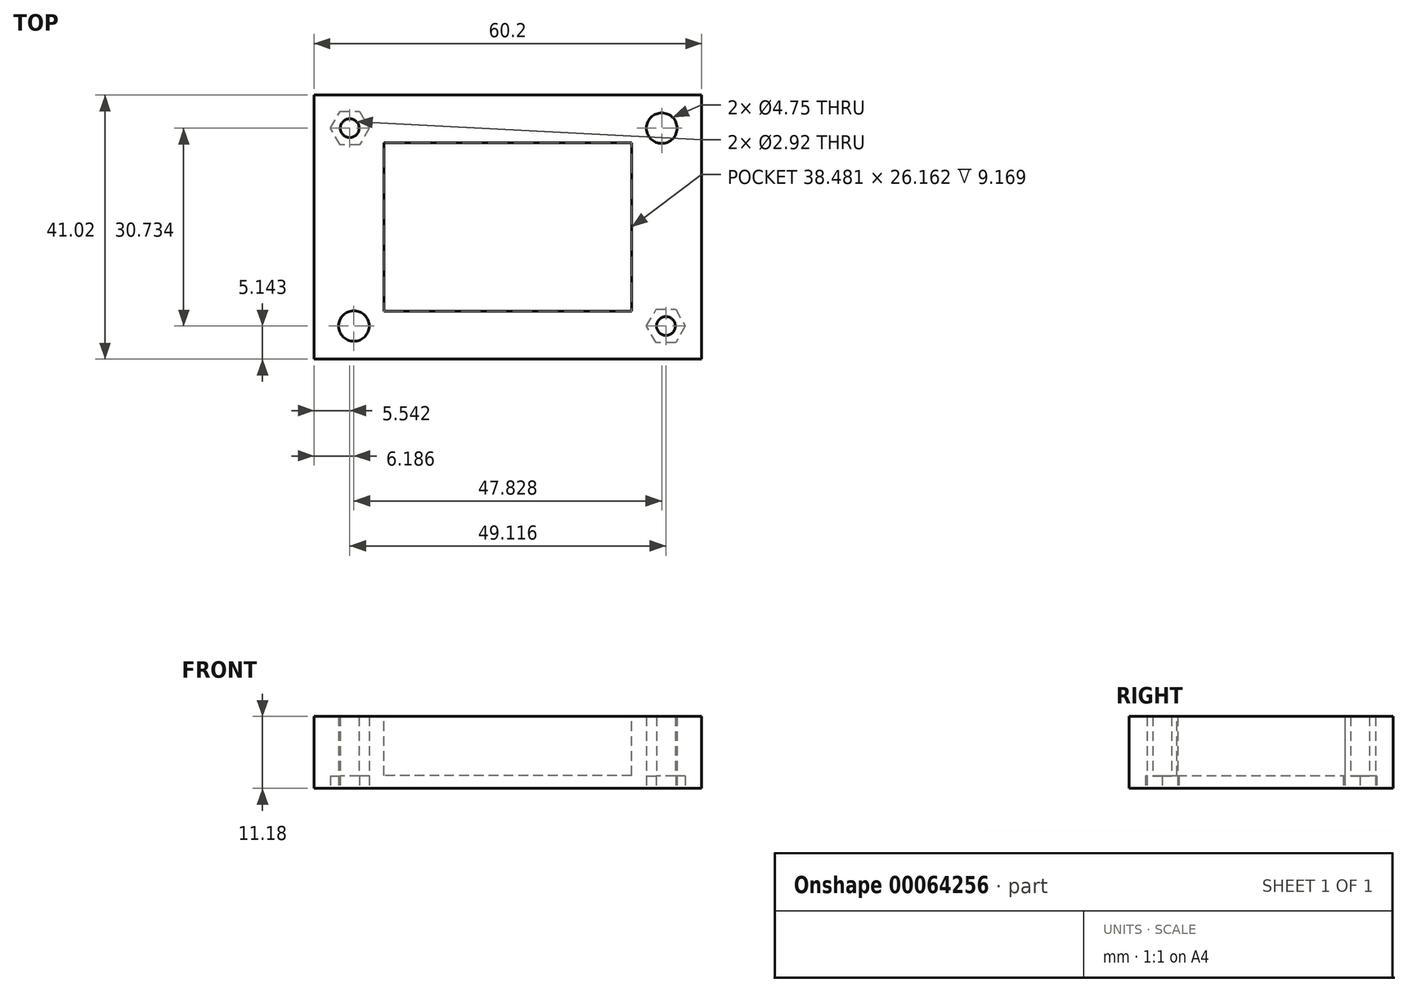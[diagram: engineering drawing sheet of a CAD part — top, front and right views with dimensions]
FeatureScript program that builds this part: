
annotation { "Feature Type Name" : "Feature", "Feature Type Description" : "" }
export const myFeature = defineFeature(function(context is Context, id is Id, definition is map)
    precondition{}
    {
        {
            var Q0;
            Q0=qCreatedBy(makeId("Top.planeOp"),FACE);
            var sketch = newSketch(context, id + "F0", { "sketchPlane" : qUnion([Q0])});
            skLineSegment(sketch, "E0.bottom", {"start": v(19.24, -13.08) * mm, "end": v(-19.24, -13.08) * mm});
            skLineSegment(sketch, "E0.top", {"start": v(19.24, 13.08) * mm, "end": v(-19.24, 13.08) * mm});
            skLineSegment(sketch, "E0.left", {"start": v(19.24, -13.08) * mm, "end": v(19.24, 13.08) * mm});
            skLineSegment(sketch, "E0.right", {"start": v(-19.24, -13.08) * mm, "end": v(-19.24, 13.08) * mm});
            skPoint(sketch, "E0.middle", {"position": v(0, 0) * mm});
            skSolve(sketch);
        }
        {
            var Q0;
            Q0=qCreatedBy(makeId("Top.planeOp"),FACE);
            var sketch = newSketch(context, id + "F1", { "sketchPlane" : qUnion([Q0])});
            skLineSegment(sketch, "E1.bottom", {"start": v(21.53, -15.37) * mm, "end": v(-21.53, -15.37) * mm});
            skLineSegment(sketch, "E1.top", {"start": v(21.53, 15.37) * mm, "end": v(-21.53, 15.37) * mm});
            skLineSegment(sketch, "E1.left", {"start": v(21.53, -15.37) * mm, "end": v(21.53, 15.37) * mm});
            skLineSegment(sketch, "E1.right", {"start": v(-21.53, -15.37) * mm, "end": v(-21.53, 15.37) * mm});
            skPoint(sketch, "E1.middle", {"position": v(0, 0) * mm});
            skSolve(sketch);
        }
        {
            var Q0;
            Q0=qCreatedBy(makeId("Top.planeOp"),FACE);
            var sketch = newSketch(context, id + "F2", { "sketchPlane" : qUnion([Q0])});
            skCircle(sketch, "E2.cCircle", {"center": v(-24.56, 15.37) * mm, "radius": 2.6 * mm, "construction": true});
            skLineSegment(sketch, "E2.0", {"start": v(-23.06, 12.76) * mm, "end": v(-26.06, 12.76) * mm});
            skLineSegment(sketch, "E2.1", {"start": v(-26.06, 12.76) * mm, "end": v(-27.56, 15.37) * mm});
            skLineSegment(sketch, "E2.2", {"start": v(-27.56, 15.37) * mm, "end": v(-26.06, 17.97) * mm});
            skLineSegment(sketch, "E2.3", {"start": v(-26.06, 17.97) * mm, "end": v(-23.06, 17.97) * mm});
            skLineSegment(sketch, "E2.4", {"start": v(-23.06, 17.97) * mm, "end": v(-21.55, 15.37) * mm});
            skLineSegment(sketch, "E2.5", {"start": v(-21.55, 15.37) * mm, "end": v(-23.06, 12.76) * mm});
            skPoint(sketch, "E2.0.midPoint", {"position": v(-24.56, 12.76) * mm});
            skSolve(sketch);
        }
        {
            var Q0;
            Q0=makeQuery(id+"F1.imprint","IMPRINT",FACE,{"disambiguationData":[TD([[makeQuery(id+"F1.imprint","IMPRINT",EDGE,{"derivedFrom":sQuery(id+"F1.wireOp",EDGE,"E1.bottom")}),-1.0]])]});
            var sketch = newSketch(context, id + "F3", { "sketchPlane" : qUnion([Q0])});
            skCircle(sketch, "E3", {"center": v(-24.56, 15.37) * mm, "radius": 1.46 * mm});
            skSolve(sketch);
        }
        {
            var Q0;
            Q0=makeQuery(id+"F1.imprint","IMPRINT",FACE,{"disambiguationData":[TD([[makeQuery(id+"F1.imprint","IMPRINT",EDGE,{"derivedFrom":sQuery(id+"F1.wireOp",EDGE,"E1.bottom")}),-1.0]])]});
            var sketch = newSketch(context, id + "F4", { "sketchPlane" : qUnion([Q0])});
            skCircle(sketch, "E4.cCircle", {"center": v(24.56, -15.37) * mm, "radius": 2.6 * mm, "construction": true});
            skLineSegment(sketch, "E4.0", {"start": v(26.06, -17.97) * mm, "end": v(23.06, -17.97) * mm});
            skLineSegment(sketch, "E4.1", {"start": v(23.06, -17.97) * mm, "end": v(21.55, -15.37) * mm});
            skLineSegment(sketch, "E4.2", {"start": v(21.55, -15.37) * mm, "end": v(23.06, -12.76) * mm});
            skLineSegment(sketch, "E4.3", {"start": v(23.06, -12.76) * mm, "end": v(26.06, -12.76) * mm});
            skLineSegment(sketch, "E4.4", {"start": v(26.06, -12.76) * mm, "end": v(27.56, -15.37) * mm});
            skLineSegment(sketch, "E4.5", {"start": v(27.56, -15.37) * mm, "end": v(26.06, -17.97) * mm});
            skPoint(sketch, "E4.0.midPoint", {"position": v(24.56, -17.97) * mm});
            skSolve(sketch);
        }
        {
            var Q0;
            Q0=makeQuery(id+"F1.imprint","IMPRINT",FACE,{"disambiguationData":[TD([[makeQuery(id+"F1.imprint","IMPRINT",EDGE,{"derivedFrom":sQuery(id+"F1.wireOp",EDGE,"E1.bottom")}),-1.0]])]});
            var sketch = newSketch(context, id + "F5", { "sketchPlane" : qUnion([Q0])});
            skCircle(sketch, "E5", {"center": v(24.56, -15.37) * mm, "radius": 1.46 * mm});
            skSolve(sketch);
        }
        {
            var Q0;
            Q0=makeQuery(id+"F1.imprint","IMPRINT",FACE,{"disambiguationData":[TD([[makeQuery(id+"F1.imprint","IMPRINT",EDGE,{"derivedFrom":sQuery(id+"F1.wireOp",EDGE,"E1.bottom")}),-1.0]])]});
            var sketch = newSketch(context, id + "F6", { "sketchPlane" : qUnion([Q0])});
            skCircle(sketch, "E6", {"center": v(-23.91, -15.37) * mm, "radius": 2.37 * mm});
            skLineSegment(sketch, "E7", {"start": v(-23.91, -15.37) * mm, "end": v(-21.53, -15.37) * mm, "construction": true});
            skSolve(sketch);
        }
        {
            var Q0;
            Q0=makeQuery(id+"F1.imprint","IMPRINT",FACE,{"disambiguationData":[TD([[makeQuery(id+"F1.imprint","IMPRINT",EDGE,{"derivedFrom":sQuery(id+"F1.wireOp",EDGE,"E1.bottom")}),-1.0]])]});
            var sketch = newSketch(context, id + "F7", { "sketchPlane" : qUnion([Q0])});
            skCircle(sketch, "E8", {"center": v(23.91, 15.37) * mm, "radius": 2.37 * mm});
            skLineSegment(sketch, "E9", {"start": v(23.91, 15.37) * mm, "end": v(21.53, 15.37) * mm, "construction": true});
            skLineSegment(sketch, "E10", {"start": v(-23.91, -15.37) * mm, "end": v(23.91, -15.37) * mm, "construction": true});
            skLineSegment(sketch, "E11", {"start": v(23.91, 15.37) * mm, "end": v(23.91, -15.37) * mm, "construction": true});
            skSolve(sketch);
        }
        {
            var Q0;
            Q0=qCreatedBy(makeId("Top.planeOp"),FACE);
            var sketch = newSketch(context, id + "F8", { "sketchPlane" : qUnion([Q0])});
            skLineSegment(sketch, "E12.bottom", {"start": v(30.1, -20.51) * mm, "end": v(-30.1, -20.51) * mm});
            skLineSegment(sketch, "E12.top", {"start": v(30.1, 20.51) * mm, "end": v(-30.1, 20.51) * mm});
            skLineSegment(sketch, "E12.left", {"start": v(30.1, -20.51) * mm, "end": v(30.1, 20.51) * mm});
            skLineSegment(sketch, "E12.right", {"start": v(-30.1, -20.51) * mm, "end": v(-30.1, 20.51) * mm});
            skPoint(sketch, "E12.middle", {"position": v(0, 0) * mm});
            skSolve(sketch);
        }
        {
            var Q0;
            Q0 = qSketchRegion(id + "F8", true);
            extrude(context, id + "F9", {"entities" : qUnion([Q0]), "depth" : 11.18 * mm, "hasOffset" : true, "offsetDistance" : 2.3 * mm});
        }
        {
            var Q0;
            Q0 = qSketchRegion(id + "F6", true);
            var Q1;
            Q1 = qSketchRegion(id + "F7", true);
            extrude(context, id + "F10", {"entities" : qUnion([Q0, Q1]), "operationType" : NewBodyOperationType.REMOVE, "depth" : 12.2 * mm, "offsetDistance" : 25.4 * mm});
        }
        {
            var Q0;
            Q0=makeQuery(id+"F9.opExtrude","CAP_FACE",FACE,{"disambiguationData":[OSD([sQuery(id+"F8.wireOp",EDGE,"E12.bottom"),sQuery(id+"F8.wireOp",EDGE,"E12.top"),sQuery(id+"F8.wireOp",EDGE,"E12.left"),sQuery(id+"F8.wireOp",EDGE,"E12.right")])],"isStart":false});
            var sketch = newSketch(context, id + "F11", { "sketchPlane" : qUnion([Q0])});
            skLineSegment(sketch, "E13.bottom", {"start": v(19.24, -13.08) * mm, "end": v(-19.24, -13.08) * mm});
            skLineSegment(sketch, "E13.top", {"start": v(19.24, 13.08) * mm, "end": v(-19.24, 13.08) * mm});
            skLineSegment(sketch, "E13.left", {"start": v(19.24, -13.08) * mm, "end": v(19.24, 13.08) * mm});
            skLineSegment(sketch, "E13.right", {"start": v(-19.24, -13.08) * mm, "end": v(-19.24, 13.08) * mm});
            skPoint(sketch, "E13.middle", {"position": v(0, 0) * mm});
            skSolve(sketch);
        }
        {
            var Q0;
            Q0=makeQuery(id+"F11.imprint","IMPRINT",FACE,{"disambiguationData":[TD([[makeQuery(id+"F11.imprint","IMPRINT",EDGE,{"derivedFrom":sQuery(id+"F11.wireOp",EDGE,"E13.bottom")}),-1.0]])]});
            extrude(context, id + "F12", {"entities" : qUnion([Q0]), "operationType" : NewBodyOperationType.REMOVE, "oppositeDirection" : true, "depth" : 9.17 * mm, "offsetDistance" : 25.4 * mm});
        }
        {
            var Q0;
            Q0 = qSketchRegion(id + "F2", true);
            extrude(context, id + "F13", {"entities" : qUnion([Q0]), "operationType" : NewBodyOperationType.REMOVE, "depth" : 1.96 * mm, "offsetDistance" : 25.4 * mm});
        }
        {
            var Q0;
            Q0 = qSketchRegion(id + "F3", true);
            var Q1;
            Q1 = qSketchRegion(id + "F5", true);
            extrude(context, id + "F14", {"entities" : qUnion([Q0, Q1]), "operationType" : NewBodyOperationType.REMOVE, "depth" : 12.2 * mm, "offsetDistance" : 25.4 * mm});
        }
        {
            var Q0;
            Q0 = qSketchRegion(id + "F4", true);
            extrude(context, id + "F15", {"entities" : qUnion([Q0]), "operationType" : NewBodyOperationType.REMOVE, "depth" : 1.96 * mm, "offsetDistance" : 25.4 * mm});
        }
    });
